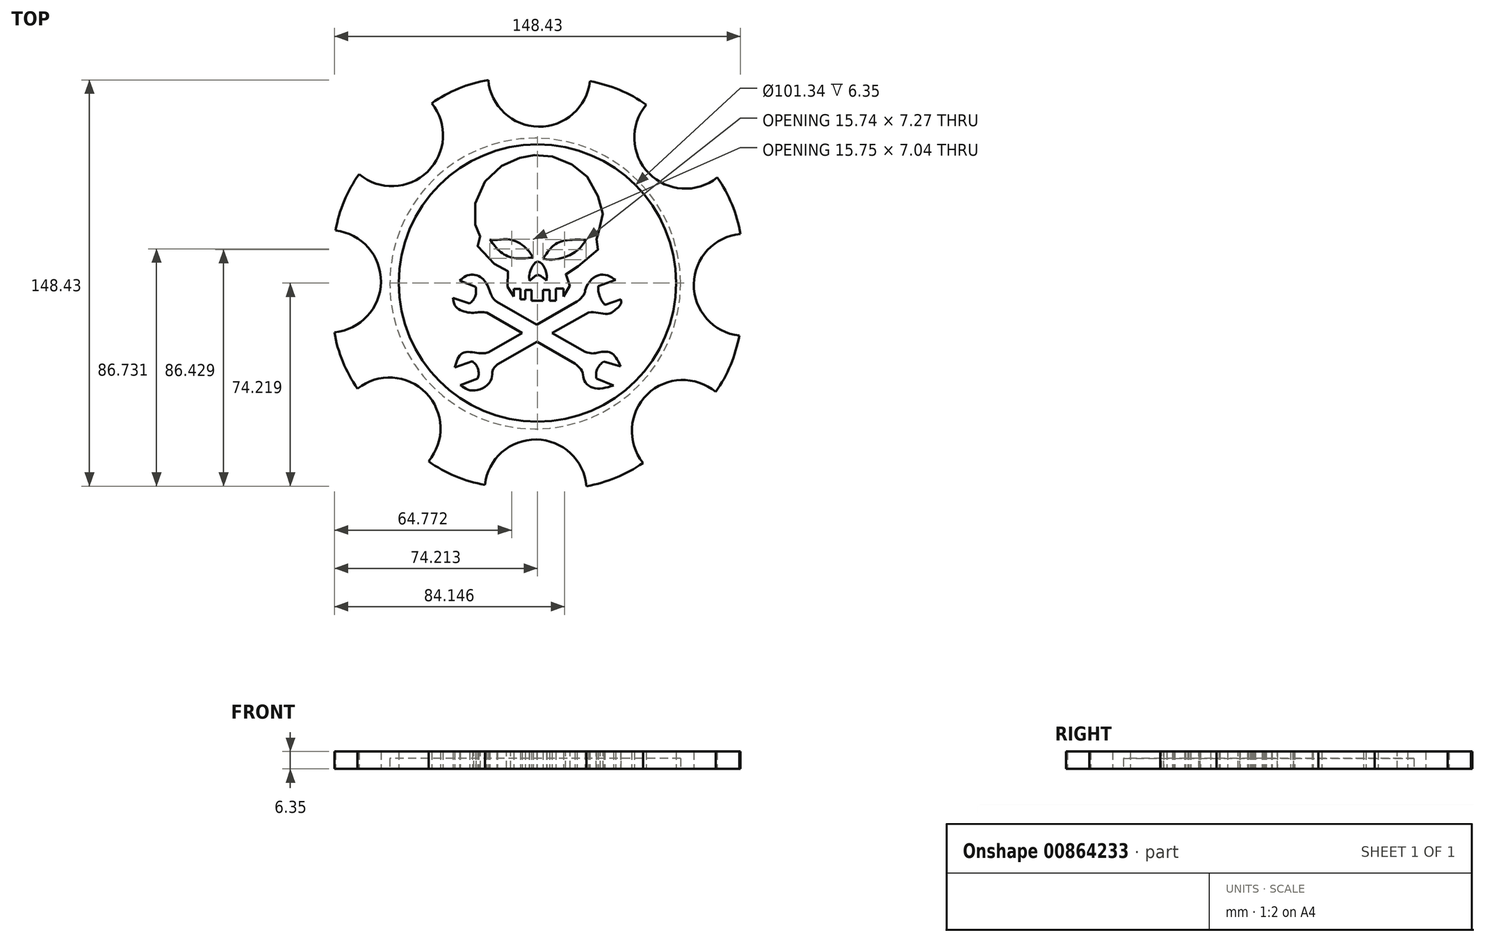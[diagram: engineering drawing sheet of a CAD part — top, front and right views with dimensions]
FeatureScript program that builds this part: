
annotation { "Feature Type Name" : "Feature", "Feature Type Description" : "" }
export const myFeature = defineFeature(function(context is Context, id is Id, definition is map)
    precondition{}
    {
        {
            var Q0;
            Q0=qCreatedBy(makeId("Top.planeOp"),FACE);
            var sketch = newSketch(context, id + "F0", { "sketchPlane" : qUnion([Q0])});
            skCircle(sketch, "E0", {"center": v(1.04, 0) * mm, "radius": 50.2 * mm});
            skLineSegment(sketch, "E1", {"start": v(-17, -25.07) * mm, "end": v(15.35, -6.58) * mm});
            skLineSegment(sketch, "E2", {"start": v(19.52, -10.55) * mm, "end": v(-13.8, -29.53) * mm});
            skLineSegment(sketch, "E3", {"start": v(18.26, -24.98) * mm, "end": v(-14.09, -6.67) * mm});
            skLineSegment(sketch, "E4", {"start": v(-17.67, -10.64) * mm, "end": v(14.58, -29.24) * mm});
            skLineSegment(sketch, "E5", {"start": v(-22.97, -28.42) * mm, "end": v(-29.42, -30.67) * mm});
            skLineSegment(sketch, "E6", {"start": v(-20.98, -34.7) * mm, "end": v(-27.32, -37.15) * mm});
            skArc(sketch, "E7", {"start": v(-20.98, -34.7) * mm, "mid": v(-20.91, -31.22) * mm, "end": v(-22.97, -28.42) * mm});
            skFitSpline(sketch, "E8", {"points": [v(-13.8, -29.53) * mm, v(-15.52, -31.76) * mm, v(-16, -34.93) * mm, v(-19.78, -38.53) * mm, v(-24.19, -38.87) * mm, v(-27.32, -37.15) * mm], "startDerivative": vector(-12.68, -11.89) * mm, "endDerivative": vector(-15.07, 10.71) * mm});
            skFitSpline(sketch, "E9", {"points": [v(-29.42, -30.67) * mm, v(-26.25, -25.32) * mm, v(-19.7, -25.5) * mm, v(-17, -25.07) * mm], "startDerivative": vector(5.7, 18.54) * mm, "endDerivative": vector(9.2, 2.97) * mm});
            skLineSegment(sketch, "E10", {"start": v(28.68, -37.24) * mm, "end": v(22.42, -34.68) * mm});
            skLineSegment(sketch, "E11", {"start": v(31.15, -30.29) * mm, "end": v(25.13, -28.56) * mm});
            skArc(sketch, "E12", {"start": v(25.13, -28.56) * mm, "mid": v(22.72, -31.15) * mm, "end": v(22.42, -34.68) * mm});
            skFitSpline(sketch, "E13", {"points": [v(28.68, -37.24) * mm, v(22, -38.32) * mm, v(18.13, -35.7) * mm, v(17.1, -32.02) * mm, v(14.58, -29.24) * mm], "startDerivative": vector(-23.15, -7.11) * mm, "endDerivative": vector(-13.7, 11.2) * mm});
            skFitSpline(sketch, "E14", {"points": [v(31.15, -30.29) * mm, v(28.68, -26.04) * mm, v(26.53, -25.01) * mm, v(23.31, -25.1) * mm, v(21.4, -25.53) * mm, v(18.26, -24.98) * mm], "startDerivative": vector(-7.78, 21.46) * mm, "endDerivative": vector(-17.92, 5.7) * mm});
            skLineSegment(sketch, "E15", {"start": v(-30.07, -5.3) * mm, "end": v(-23.98, -7.32) * mm});
            skLineSegment(sketch, "E16", {"start": v(-27.57, 1.06) * mm, "end": v(-21.82, -1.24) * mm});
            skArc(sketch, "E17", {"start": v(-23.98, -7.32) * mm, "mid": v(-21.91, -4.63) * mm, "end": v(-21.82, -1.24) * mm});
            skFitSpline(sketch, "E18", {"points": [v(-30.07, -5.3) * mm, v(-27.57, -9.55) * mm, v(-23.03, -10.7) * mm, v(-20, -10.43) * mm, v(-17.67, -10.64) * mm], "startDerivative": vector(2.1, -25.87) * mm, "endDerivative": vector(11.5, -1.77) * mm});
            skFitSpline(sketch, "E19", {"points": [v(-27.57, 1.06) * mm, v(-24.32, 3.1) * mm, v(-20.33, 2.55) * mm, v(-17.83, 0) * mm, v(-16.14, -3.87) * mm], "startDerivative": vector(12.12, 10.4) * mm, "endDerivative": vector(5.83, -15.65) * mm});
            skFitSpline(sketch, "E20", {"points": [v(-16.14, -3.87) * mm, v(-15.46, -5.3) * mm, v(-14.09, -6.67) * mm], "startDerivative": vector(1.15, -3.1) * mm, "endDerivative": vector(2.92, -2.52) * mm});
            skLineSegment(sketch, "E21", {"start": v(23.06, -0.93) * mm, "end": v(29.35, 1.29) * mm});
            skLineSegment(sketch, "E22", {"start": v(25.48, -7.74) * mm, "end": v(31.3, -5.7) * mm});
            skArc(sketch, "E23", {"start": v(23.06, -0.93) * mm, "mid": v(23.55, -4.6) * mm, "end": v(25.48, -7.74) * mm});
            skFitSpline(sketch, "E24", {"points": [v(29.35, 1.29) * mm, v(25.95, 3.09) * mm, v(21.65, 2.38) * mm, v(18.48, -1.78) * mm, v(17.91, -3.86) * mm, v(15.35, -6.58) * mm], "startDerivative": vector(-15.88, 11.03) * mm, "endDerivative": vector(-16.1, -14.09) * mm});
            skFitSpline(sketch, "E25", {"points": [v(31.3, -5.7) * mm, v(31.3, -7.36) * mm, v(29.35, -9.54) * mm, v(26.37, -11.1) * mm, v(19.52, -10.55) * mm], "startDerivative": vector(1.81, -9.21) * mm, "endDerivative": vector(-19.75, -2.97) * mm});
            skFitSpline(sketch, "E26", {"points": [v(-16.5, 16.08) * mm, v(-8.8, 16.04) * mm, v(-0.75, 9.54) * mm], "startDerivative": vector(14.88, -3.13) * mm, "endDerivative": vector(9.8, -17.55) * mm});
            skFitSpline(sketch, "E27", {"points": [v(-16.5, 16.08) * mm, v(-13.06, 11.91) * mm, v(-8.16, 9.4) * mm, v(-0.75, 9.54) * mm], "startDerivative": vector(10.06, -14.16) * mm, "endDerivative": vector(21.15, 2.37) * mm});
            skFitSpline(sketch, "E28", {"points": [v(2.88, 9.08) * mm, v(5.99, 13.18) * mm, v(9.9, 15.5) * mm, v(18.61, 15.98) * mm], "startDerivative": vector(9.63, 14.34) * mm, "endDerivative": vector(23.97, -0.5) * mm});
            skFitSpline(sketch, "E29", {"points": [v(18.61, 15.98) * mm, v(16.42, 13.02) * mm, v(12.63, 10.41) * mm, v(2.88, 9.08) * mm], "startDerivative": vector(-7.6, -11.42) * mm, "endDerivative": vector(-26.7, 6.15) * mm});
            skFitSpline(sketch, "E30", {"points": [v(-2.05, 1.08) * mm, v(-2, 3.98) * mm, v(0.94, 8) * mm, v(3.99, 4.38) * mm, v(4.13, 1.14) * mm], "startDerivative": vector(-1.9, 11.55) * mm, "endDerivative": vector(-1.3, -12.45) * mm});
            skLineSegment(sketch, "E31", {"start": v(-1.27, -6.3) * mm, "end": v(2.84, -6.3) * mm});
            skLineSegment(sketch, "E32", {"start": v(2.84, -6.3) * mm, "end": v(2.84, -2.35) * mm});
            skLineSegment(sketch, "E33", {"start": v(2.84, -2.35) * mm, "end": v(5.25, -2.35) * mm});
            skLineSegment(sketch, "E34", {"start": v(5.25, -2.35) * mm, "end": v(5.25, -6.3) * mm});
            skLineSegment(sketch, "E35", {"start": v(5.25, -6.3) * mm, "end": v(7.53, -6.3) * mm});
            skLineSegment(sketch, "E36", {"start": v(7.53, -6.3) * mm, "end": v(7.53, -1.8) * mm});
            skLineSegment(sketch, "E37", {"start": v(7.53, -1.8) * mm, "end": v(10.41, -1.8) * mm});
            skLineSegment(sketch, "E38", {"start": v(10.41, -1.8) * mm, "end": v(10.41, -4.8) * mm});
            skLineSegment(sketch, "E39", {"start": v(-1.27, -6.3) * mm, "end": v(-1.27, -2.35) * mm});
            skLineSegment(sketch, "E40", {"start": v(-1.27, -2.35) * mm, "end": v(-3.64, -2.35) * mm});
            skLineSegment(sketch, "E41", {"start": v(-3.64, -2.35) * mm, "end": v(-3.64, -5.8) * mm});
            skLineSegment(sketch, "E42", {"start": v(-3.64, -5.8) * mm, "end": v(-5.4, -5.8) * mm});
            skLineSegment(sketch, "E43", {"start": v(-5.4, -5.8) * mm, "end": v(-5.4, -1.92) * mm});
            skLineSegment(sketch, "E44", {"start": v(-5.4, -1.92) * mm, "end": v(-7.79, -1.92) * mm});
            skLineSegment(sketch, "E45", {"start": v(-7.79, -1.92) * mm, "end": v(-7.79, -4.8) * mm});
            skFitSpline(sketch, "E46", {"points": [v(-7.79, -4.8) * mm, v(-10.44, -3.51) * mm, v(-8.99, 3.45) * mm, v(-10.96, 4.86) * mm, v(-15.67, 7.88) * mm, v(-21.47, 14.9) * mm, v(-20.42, 16.12) * mm, v(-20.36, 19.07) * mm, v(-21.98, 21.8) * mm, v(-21.54, 30.85) * mm, v(-16.13, 39.9) * mm, v(-8.83, 44.86) * mm, v(-3.18, 46.44) * mm, v(0.66, 46.98) * mm, v(7.39, 46.12) * mm, v(14.89, 42.6) * mm, v(20, 37.75) * mm, v(23.95, 29.22) * mm, v(24.7, 24.06) * mm, v(23.06, 19.09) * mm, v(22.5, 18.15) * mm, v(22.5, 16.15) * mm, v(23.83, 14.77) * mm, v(19.18, 8.57) * mm, v(11.49, 3.97) * mm, v(11.2, 3.33) * mm, v(12.13, 1.07) * mm, v(12.66, -2.4) * mm, v(10.41, -4.8) * mm], "startDerivative": vector(-129.77, 14.06) * mm, "endDerivative": vector(-120.88, -19.37) * mm});
            skFitSpline(sketch, "E47", {"points": [v(-2.05, 1.08) * mm, v(-0.7, 2.18) * mm, v(1, 3.12) * mm, v(2.89, 2.15) * mm, v(4.13, 1.14) * mm], "startDerivative": vector(5.37, 4.29) * mm, "endDerivative": vector(4.9, -4.05) * mm});
            skSolve(sketch);
        }
        {
            var Q0;
            Q0=qCreatedBy(makeId("Top.planeOp"),FACE);
            var sketch = newSketch(context, id + "F1", { "sketchPlane" : qUnion([Q0])});
            skArc(sketch, "E48", {"start": v(-64.36, 39.96) * mm, "mid": v(-69.78, 30.14) * mm, "end": v(-72.94, 19.38) * mm});
            skArc(sketch, "E49.1.0", {"start": v(-73.4, -17.77) * mm, "mid": v(-70.3, -28.55) * mm, "end": v(-64.92, -38.4) * mm});
            skArc(sketch, "E49.2.0", {"start": v(-38.97, -65) * mm, "mid": v(-29.15, -70.42) * mm, "end": v(-18.39, -73.58) * mm});
            skPoint(sketch, "E49.center", {"position": v(0.81, 0.18) * mm});
            skArc(sketch, "E50.3.3.0", {"start": v(18.76, -74.04) * mm, "mid": v(29.54, -70.93) * mm, "end": v(39.39, -65.55) * mm});
            skArc(sketch, "E50.3.4.0", {"start": v(65.98, -39.6) * mm, "mid": v(71.4, -29.79) * mm, "end": v(74.57, -19.02) * mm});
            skArc(sketch, "E50.3.5.0", {"start": v(75.03, 18.13) * mm, "mid": v(71.92, 28.9) * mm, "end": v(66.54, 38.76) * mm});
            skArc(sketch, "E50.3.6.0", {"start": v(40.6, 65.35) * mm, "mid": v(30.78, 70.77) * mm, "end": v(20.01, 73.93) * mm});
            skArc(sketch, "E50.3.7.0", {"start": v(-17.14, 74.4) * mm, "mid": v(-27.92, 71.29) * mm, "end": v(-37.76, 65.9) * mm});
            skArc(sketch, "E51", {"start": v(-38.97, -65) * mm, "mid": v(-39.9, -39.95) * mm, "end": v(-64.92, -38.4) * mm});
            skArc(sketch, "E52.1.0", {"start": v(18.76, -74.04) * mm, "mid": v(0.4, -57) * mm, "end": v(-18.39, -73.58) * mm});
            skArc(sketch, "E52.2.0", {"start": v(65.98, -39.6) * mm, "mid": v(40.94, -40.54) * mm, "end": v(39.39, -65.55) * mm});
            skArc(sketch, "E52.3.0", {"start": v(75.03, 18.13) * mm, "mid": v(57.98, -0.24) * mm, "end": v(74.57, -19.02) * mm});
            skArc(sketch, "E52.4.0", {"start": v(40.6, 65.35) * mm, "mid": v(41.53, 40.31) * mm, "end": v(66.54, 38.76) * mm});
            skArc(sketch, "E52.5.0", {"start": v(-17.14, 74.4) * mm, "mid": v(1.23, 57.35) * mm, "end": v(20.01, 73.93) * mm});
            skArc(sketch, "E52.6.0", {"start": v(-64.36, 39.96) * mm, "mid": v(-39.32, 40.9) * mm, "end": v(-37.76, 65.9) * mm});
            skArc(sketch, "E52.7.0", {"start": v(-73.4, -17.77) * mm, "mid": v(-56.36, 0.6) * mm, "end": v(-72.94, 19.38) * mm});
            skCircle(sketch, "E53", {"center": v(0.81, 0.18) * mm, "radius": 50.67 * mm});
            skSolve(sketch);
        }
        {
            var Q0;
            Q0=makeQuery(id+"F0.imprint","IMPRINT",FACE,{"disambiguationData":[TD([[makeQuery(id+"F0.imprint","IMPRINT",EDGE,{"derivedFrom":sQuery(id+"F0.wireOp",EDGE,"E5")}),-1.0]])]});
            var Q1;
            {var subQ0=sQuery(id+"F0.wireOp",EDGE,"E4");var subQ1=sQuery(id+"F0.wireOp",EDGE,"E1");var subQ2=makeQuery(id+"F0.imprint","INTERSECT",VERTEX,{"derivedFrom":[subQ1,subQ0]});Q1=makeQuery(id+"F0.imprint","IMPRINT",FACE,{"disambiguationData":[TD([[makeQuery(id+"F0.imprint","IMPRINT",EDGE,{"disambiguationData":[TD([[subQ2,-1.0]])],"derivedFrom":subQ1}),-1.0]])]});}
            var Q2;
            Q2=makeQuery(id+"F0.imprint","IMPRINT",FACE,{"disambiguationData":[TD([[makeQuery(id+"F0.imprint","IMPRINT",EDGE,{"derivedFrom":sQuery(id+"F0.wireOp",EDGE,"E21")}),1.0]])]});
            var Q3;
            Q3=makeQuery(id+"F0.imprint","IMPRINT",FACE,{"disambiguationData":[TD([[makeQuery(id+"F0.imprint","IMPRINT",EDGE,{"derivedFrom":sQuery(id+"F0.wireOp",EDGE,"E15")}),-1.0]])]});
            var Q4;
            Q4=makeQuery(id+"F0.imprint","IMPRINT",FACE,{"disambiguationData":[TD([[makeQuery(id+"F0.imprint","IMPRINT",EDGE,{"derivedFrom":sQuery(id+"F0.wireOp",EDGE,"E10")}),1.0]])]});
            var Q5;
            Q5=makeQuery(id+"F0.imprint","IMPRINT",FACE,{"disambiguationData":[TD([[makeQuery(id+"F0.imprint","IMPRINT",EDGE,{"derivedFrom":sQuery(id+"F0.wireOp",EDGE,"E26")}),1.0]])]});
            extrude(context, id + "F2", {"entities" : qUnion([Q0, Q1, Q2, Q3, Q4, Q5]), "depth" : 6.35 * mm, "offsetDistance" : 25.4 * mm});
        }
        {
            var Q0;
            Q0=makeQuery(id+"F1.imprint","IMPRINT",FACE,{"disambiguationData":[TD([[makeQuery(id+"F1.imprint","IMPRINT",EDGE,{"derivedFrom":sQuery(id+"F1.wireOp",EDGE,"E48")}),1.0]])]});
            extrude(context, id + "F3", {"entities" : qUnion([Q0]), "depth" : 6.35 * mm, "offsetDistance" : 25.4 * mm});
        }
        {
            var Q0;
            Q0=qCreatedBy(makeId("Top.planeOp"),FACE);
            var sketch = newSketch(context, id + "F4", { "sketchPlane" : qUnion([Q0])});
            skCircle(sketch, "E54", {"center": v(0, 0) * mm, "radius": 53.13 * mm});
            skSolve(sketch);
        }
        {
            var Q0;
            Q0=makeQuery(id+"F4.imprint","IMPRINT",FACE,{"disambiguationData":[TD([[makeQuery(id+"F4.imprint","IMPRINT",EDGE,{"derivedFrom":sQuery(id+"F4.wireOp",EDGE,"E54")}),1.0]])]});
            extrude(context, id + "F5", {"entities" : qUnion([Q0]), "depth" : 3.8 * mm, "offsetDistance" : 25.4 * mm});
        }
    });
